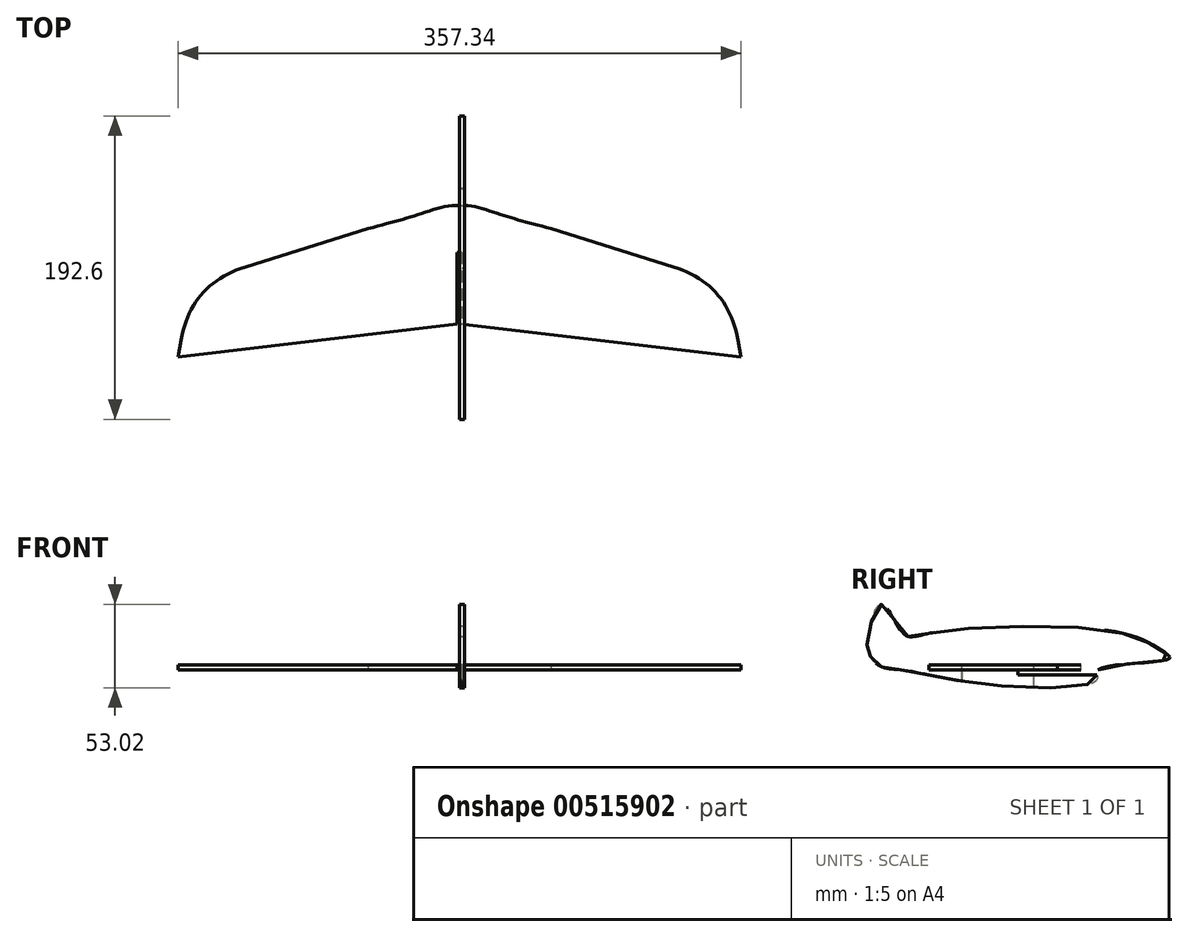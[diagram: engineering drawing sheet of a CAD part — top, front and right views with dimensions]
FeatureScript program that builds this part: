
annotation { "Feature Type Name" : "Feature", "Feature Type Description" : "" }
export const myFeature = defineFeature(function(context is Context, id is Id, definition is map)
    precondition{}
    {
        {
            var Q0;
            Q0=qCreatedBy(makeId("Right.planeOp"),FACE);
            var sketch = newSketch(context, id + "F0", { "sketchPlane" : qUnion([Q0])});
            skFitSpline(sketch, "E0", {"points": [v(-56.59, 23.42) * mm, v(-38.98, 23.42) * mm, v(79.22, 24.05) * mm, v(108.15, 12.1) * mm, v(112.55, 7.07) * mm, v(67.28, 0) * mm, v(66.65, -6.13) * mm, v(-3.14, -9.27) * mm, v(-57.85, 0) * mm, v(-71.68, 2.67) * mm, v(-78.6, 10.85) * mm, v(-79.22, 19.02) * mm, v(-70.42, 41.66) * mm, v(-56.59, 23.42) * mm]});
            skSolve(sketch);
        }
        {
            var Q0;
            Q0 = qSketchRegion(id + "F0", true);
            extrude(context, id + "F1", {"entities" : qUnion([Q0]), "depth" : 3.17 * mm, "offsetDistance" : 25.4 * mm});
        }
        {
            var Q0;
            Q0=makeQuery(id+"F1.opExtrude","CAP_FACE",FACE,{"disambiguationData":[OSD([sQuery(id+"F0.wireOp",EDGE,"E0")])],"isStart":false});
            var sketch = newSketch(context, id + "F2", { "sketchPlane" : qUnion([Q0])});
            skLineSegment(sketch, "E1.bottom", {"start": v(67.28, 0) * mm, "end": v(16.48, 0) * mm});
            skLineSegment(sketch, "E1.top", {"start": v(67.28, -3.17) * mm, "end": v(16.48, -3.18) * mm});
            skLineSegment(sketch, "E1.left", {"start": v(67.28, 0) * mm, "end": v(67.28, -3.17) * mm});
            skLineSegment(sketch, "E1.right", {"start": v(16.48, 0) * mm, "end": v(16.48, -3.18) * mm});
            skSolve(sketch);
        }
        {
            var Q0;
            Q0 = qSketchRegion(id + "F2", true);
            extrude(context, id + "F3", {"entities" : qUnion([Q0]), "operationType" : NewBodyOperationType.REMOVE, "endBound" : BoundingType.UP_TO_NEXT, "oppositeDirection" : true, "depth" : 25.4 * mm, "offsetDistance" : 25.4 * mm});
        }
        {
            var Q0;
            Q0=qCreatedBy(makeId("Top.planeOp"),FACE);
            var sketch = newSketch(context, id + "F4", { "sketchPlane" : qUnion([Q0])});
            skFitSpline(sketch, "E2", {"points": [v(0, 56.17) * mm, v(-26.2, 50.46) * mm, v(-58, 41.49) * mm], "startDerivative": vector(-52.5, 5.19) * mm, "endDerivative": vector(-72.16, -20.23) * mm});
            skLineSegment(sketch, "E3", {"start": v(-58, 41.49) * mm, "end": v(-170.52, 6.43) * mm});
            skLineSegment(sketch, "E4", {"start": v(-170.52, 6.43) * mm, "end": v(-178.67, -40.05) * mm});
            skLineSegment(sketch, "E5", {"start": v(-178.67, -40.05) * mm, "end": v(0, -18.85) * mm});
            skLineSegment(sketch, "E6.MirrorCS", {"start": v(58, 41.49) * mm, "end": v(170.52, 6.43) * mm});
            skFitSpline(sketch, "E7.MirrorCS", {"points": [v(0, 56.17) * mm, v(26.2, 50.46) * mm, v(58, 41.49) * mm], "startDerivative": vector(52.5, 5.19) * mm, "endDerivative": vector(72.16, -20.23) * mm});
            skLineSegment(sketch, "E8.MirrorCS", {"start": v(178.67, -40.05) * mm, "end": v(0, -18.85) * mm});
            skLineSegment(sketch, "E9.MirrorCS", {"start": v(170.52, 6.43) * mm, "end": v(178.67, -40.05) * mm});
            skSolve(sketch);
        }
        {
            var Q0;
            Q0 = qSketchRegion(id + "F4", true);
            extrude(context, id + "F5", {"entities" : qUnion([Q0]), "depth" : 3.17 * mm, "offsetDistance" : 25.4 * mm});
        }
        {
            var Q0;
            Q0=makeQuery(id+"F5.opExtrude","CAP_FACE",FACE,{"disambiguationData":[OSD([sQuery(id+"F4.wireOp",EDGE,"E2"),sQuery(id+"F4.wireOp",EDGE,"E3"),sQuery(id+"F4.wireOp",EDGE,"E4"),sQuery(id+"F4.wireOp",EDGE,"E5"),sQuery(id+"F4.wireOp",EDGE,"E6.MirrorCS"),sQuery(id+"F4.wireOp",EDGE,"E7.MirrorCS"),sQuery(id+"F4.wireOp",EDGE,"E8.MirrorCS"),sQuery(id+"F4.wireOp",EDGE,"E9.MirrorCS")])],"isStart":false});
            var sketch = newSketch(context, id + "F6", { "sketchPlane" : qUnion([Q0])});
            skLineSegment(sketch, "E10.bottom", {"start": v(1.59, 26.42) * mm, "end": v(-1.59, 26.42) * mm});
            skLineSegment(sketch, "E10.top", {"start": v(1.59, -20.71) * mm, "end": v(-1.59, -20.71) * mm});
            skLineSegment(sketch, "E10.left", {"start": v(1.59, 26.42) * mm, "end": v(1.59, -20.71) * mm});
            skLineSegment(sketch, "E10.right", {"start": v(-1.59, 26.42) * mm, "end": v(-1.59, -20.71) * mm});
            skPoint(sketch, "E10.middle", {"position": v(0, 2.85) * mm});
            skSolve(sketch);
        }
        {
            var Q0;
            {var subQ6=sQuery(id+"F6.wireOp",EDGE,"E10.bottom");Q0=makeQuery(id+"F6.imprint","IMPRINT",FACE,{"disambiguationData":[TD([[makeQuery(id+"F6.imprint","IMPRINT",EDGE,{"derivedFrom":subQ6}),1.0]])]});}
            extrude(context, id + "F7", {"entities" : qUnion([Q0]), "operationType" : NewBodyOperationType.REMOVE, "oppositeDirection" : true, "depth" : 25.4 * mm, "offsetDistance" : 25.4 * mm});
        }
        {
            var Q0;
            Q0=makeQuery(id+"F5.opExtrude","SWEPT_EDGE",EDGE,{"disambiguationData":[OSD([sQuery(id+"F4.wireOp",EDGE,"E3"),sQuery(id+"F4.wireOp",EDGE,"E4")])]});
            var Q1;
            Q1=makeQuery(id+"F5.opExtrude","SWEPT_EDGE",EDGE,{"disambiguationData":[OSD([sQuery(id+"F4.wireOp",EDGE,"E6.MirrorCS"),sQuery(id+"F4.wireOp",EDGE,"E9.MirrorCS")])]});
            fillet(context, id + "F8", {"entities" : qUnion([Q0, Q1]), "radius" : 59.34 * mm, "tangentPropagation" : true, "rho" : 0.5, "crossSection" : FilletCrossSection.CONIC, "allowEdgeOverflow" : false});
        }
    });
